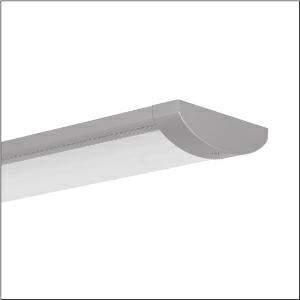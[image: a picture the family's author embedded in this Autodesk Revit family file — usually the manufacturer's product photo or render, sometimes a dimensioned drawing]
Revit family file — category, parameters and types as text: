
# Revit family: tv_20_5xa861d4n0j
name_source: partatom
category: Lighting Fixtures
units: mm (PartAtom-declared; Revit-internal decimal feet)

## family parameters
Cut with Voids When Loaded = No
Host = Face
Light Source = No
Part Type = Normal
Room Calculation Point = No
Round Connector Dimension = Use Diameter
Shared = No

## types (1)
- TV 20 (1 x LED 4000K / CRI = 80 (unbekannt), 3960 lm, 4000K)
    Apparent Load = 37 VA
    CIE Flux Codes = 48 78 95 99 100
    Color Rendering = 80
    Color Temperature = 4000K
    Default Elevation = 1800 mm
    Description = TV 20, vandal-proof luminaire, primary light control with specular reflector, of aluminium, matt, primary optical cover: enclosure, of PC, frosted, light emission: direct distribution, primary light characteristic: symmetric, installation type: surface-mounted, LED, rated luminous flux: 3.960lm, luminous efficacy: 107lm/W, light colour: 840, colour temperature: 4000K, control gear: ECG DALI, mains connection: 230V, AC, 50Hz, rated input power: 37W, luminaire housing, of aluminium, coated, Siteco® metallic grey (DB 702S), with wall and ceiling fixing element, length: 1.261mm, width: 260mm, height: 70mm, protection rating (complete): IP65, insulation class (complete): insulation class I (protective earthing), certification: CE, protection symbol: F, impact resistance: 2x IK10, standard: EN 60598, packaging unit: 1 piece
    Height = 70 mm
    Lamp = 1 x LED 4000K / CRI >= 80 (unbekannt)
    Lamp Light Flux = 3960 lm
    Lamp count = 1
    Length = 1261 mm
    Luminous efficacy = 107 lm/W
    Manufacturer = Siteco
    ModVariant = No
    Model = 5XA861D4N0J
    Mounting Place = Ceiling
    Mounting Type = Surface mounted
    Number of Poles = 1
    OnlyDefault = Yes
    Power Factor = 1
    Product Name = TV 20
    Product group = vandal-proof luminaire
    ProductGroupID = 307
    Protection Class = Protection class I
    Protection Degree = IP 65
    RLX_Detail_Level = 1
    RLX_Emergency_Light_Flux = 0 lm
    RLX_Emergency_Type = 0
    RLX_Emergency_Type_DB = No
    RlxData = <blob elided: 25605 chars, md5=633e9030>
    Socket = socket
    Standby Power = 0 W
    System Light Flux = 3960 lm
    System Power = 37 W
    Type Comments = Product without accessories
    Type Image = l_1004809.jpg
    URL = http://relux.com
    VarID = ---
    Voltage = 0 V
    Weight = 0.00 kg
    Width = 260 mm

## geometry (parser evidence)
native form markers: Blend x4, Sweep x10
no freeform markers — native parametric forms only
